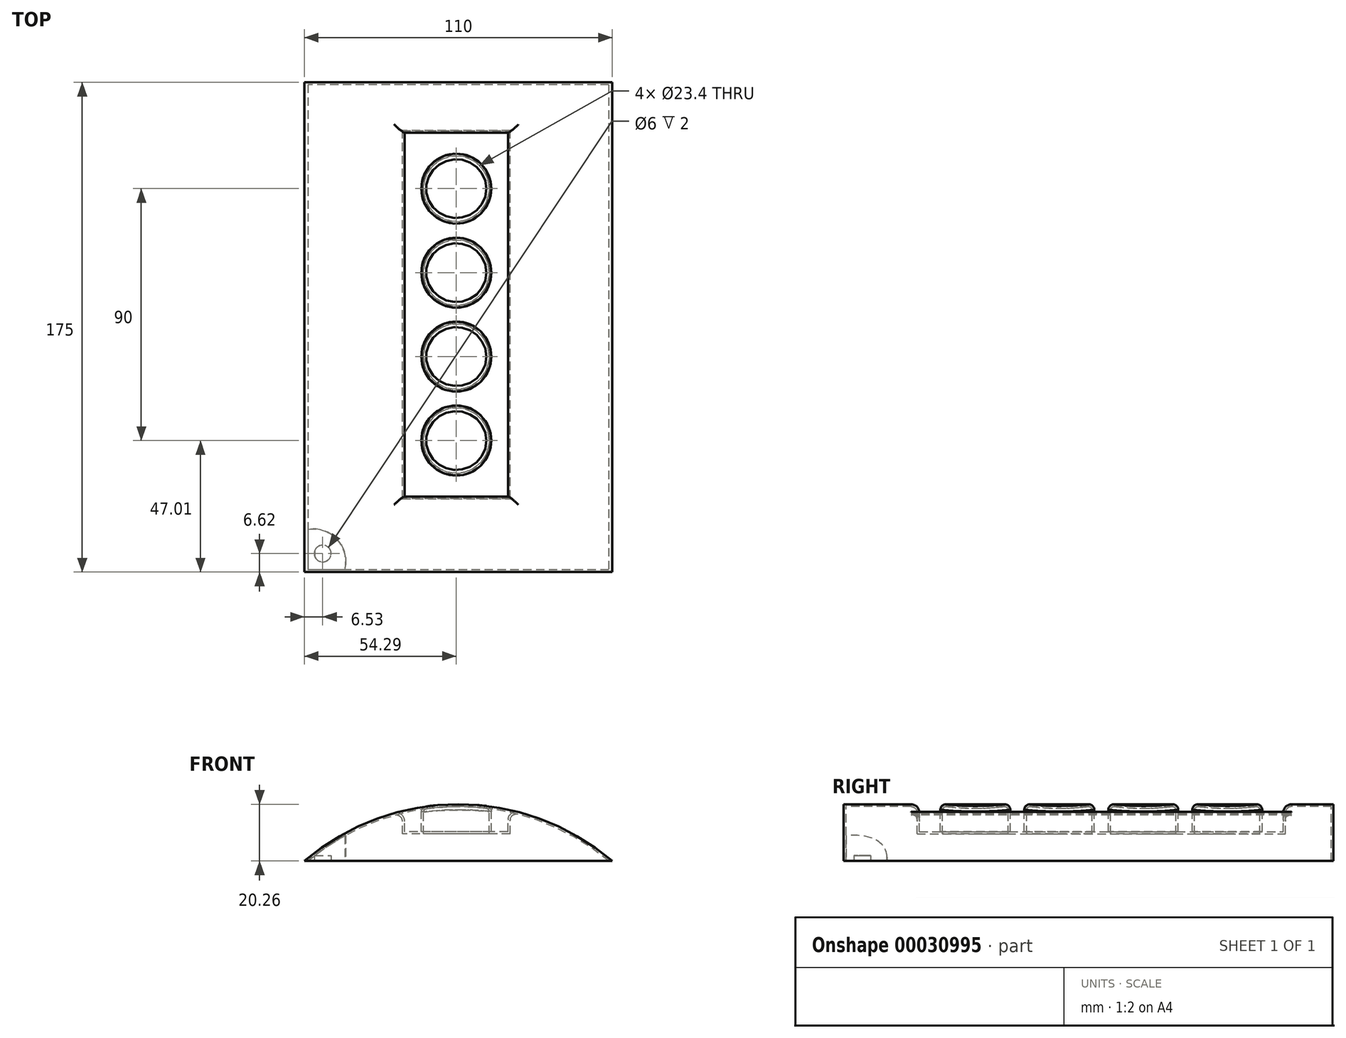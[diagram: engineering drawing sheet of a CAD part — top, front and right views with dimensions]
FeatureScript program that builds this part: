
annotation { "Feature Type Name" : "Feature", "Feature Type Description" : "" }
export const myFeature = defineFeature(function(context is Context, id is Id, definition is map)
    precondition{}
    {
        {
            var Q0;
            Q0=qCreatedBy(makeId("Front.planeOp"),FACE);
            var sketch = newSketch(context, id + "F9", { "sketchPlane" : qUnion([Q0])});
            skLineSegment(sketch, "E0", {"start": v(55.71, 0) * mm, "end": v(-54.29, 0) * mm});
            skLineSegment(sketch, "E1.top", {"start": v(55.71, 20.45) * mm, "end": v(-54.29, 20.45) * mm});
            skLineSegment(sketch, "E1.left", {"start": v(55.71, 0) * mm, "end": v(55.71, 20.45) * mm});
            skLineSegment(sketch, "E1.right", {"start": v(-54.29, 0) * mm, "end": v(-54.29, 20.45) * mm});
            skSolve(sketch);
        }
        {
            var Q0;
            Q0 = qSketchRegion(id + "F9", true);
            extrude(context, id + "F0", {"entities" : qUnion([Q0]), "depth" : 175 * mm});
        }
        {
            var Q0;
            Q0=makeQuery(id+"F0.opExtrude","SWEPT_FACE",FACE,{"disambiguationData":[OSD([sQuery(id+"F9.wireOp",EDGE,"E1.top")])]});
            var sketch = newSketch(context, id + "F1", { "sketchPlane" : qUnion([Q0])});
            skPoint(sketch, "E2.rect.middle", {"position": v(0, -82.99) * mm});
            skLineSegment(sketch, "E3.rect.bottom", {"start": v(18.44, -147.99) * mm, "end": v(-18.44, -147.99) * mm});
            skLineSegment(sketch, "E3.rect.top", {"start": v(18.44, -17.99) * mm, "end": v(-18.44, -17.99) * mm});
            skLineSegment(sketch, "E3.rect.left", {"start": v(18.44, -147.99) * mm, "end": v(18.44, -17.99) * mm});
            skLineSegment(sketch, "E3.rect.right", {"start": v(-18.44, -147.99) * mm, "end": v(-18.44, -17.99) * mm});
            skPoint(sketch, "E2.rect.top.start.orphan", {"position": v(25.94, -17.26) * mm});
            skPoint(sketch, "E2.rect.right.end.orphan", {"position": v(-25.94, -17.26) * mm});
            skPoint(sketch, "E2.rect.bottom.end.orphan", {"position": v(-25.94, -148.72) * mm});
            skPoint(sketch, "E2.rect.bottom.start.orphan", {"position": v(25.94, -148.72) * mm});
            skCircle(sketch, "E4", {"center": v(0, -37.99) * mm, "radius": 12.5 * mm});
            skCircle(sketch, "E5", {"center": v(0, -67.99) * mm, "radius": 12.5 * mm});
            skCircle(sketch, "E6", {"center": v(0, -97.99) * mm, "radius": 12.5 * mm});
            skCircle(sketch, "E7", {"center": v(0, -127.99) * mm, "radius": 12.5 * mm});
            skSolve(sketch);
        }
        {
            var Q0;
            Q0=makeQuery(id+"F1.imprint","IMPRINT",FACE,{"disambiguationData":[TD([[makeQuery(id+"F1.imprint","IMPRINT",EDGE,{"derivedFrom":sQuery(id+"F1.wireOp",EDGE,"E3.rect.bottom")}),-1.0]])]});
            extrude(context, id + "F10", {"entities" : qUnion([Q0]), "operationType" : NewBodyOperationType.REMOVE, "oppositeDirection" : true, "depth" : 10 * mm});
        }
        {
            var Q0;
            Q0=makeQuery(id+"F0.opExtrude","CAP_FACE",FACE,{"disambiguationData":[OSD([sQuery(id+"F9.wireOp",EDGE,"E0"),sQuery(id+"F9.wireOp",EDGE,"E1.top"),sQuery(id+"F9.wireOp",EDGE,"E1.left"),sQuery(id+"F9.wireOp",EDGE,"E1.right")])],"isStart":false});
            var sketch = newSketch(context, id + "F2", { "sketchPlane" : qUnion([Q0])});
            skArc(sketch, "E8", {"start": v(55.71, 0) * mm, "mid": v(0.71, 20.26) * mm, "end": v(-54.29, 0) * mm});
            skSolve(sketch);
        }
        {
            var Q0;
            Q0 = qSketchRegion(id + "F2", true);
            var Q1;
            Q1=makeQuery(id+"F2.imprint","IMPRINT",FACE,{"disambiguationData":[TD([[makeQuery(id+"F2.imprint","IMPRINT",EDGE,{"derivedFrom":sQuery(id+"F2.wireOp",EDGE,"E8")}),-1.0]])]});
            extrude(context, id + "F11", {"entities" : qUnion([Q0, Q1]), "operationType" : NewBodyOperationType.REMOVE, "endBound" : BoundingType.THROUGH_ALL, "oppositeDirection" : true, "depth" : 25 * mm});
        }
        {
            var Q0;
            Q0=makeQuery(id+"F11.boolean.opBoolean","INTERSECT",EDGE,{"derivedFrom":[makeQuery(id+"F10.boolean.opBoolean","COPY",FACE,{"derivedFrom":makeQuery(id+"F10.opExtrude","SWEPT_FACE",FACE,{"disambiguationData":[OSD([sQuery(id+"F1.wireOp",EDGE,"E3.rect.right")])]})}),makeQuery(id+"F11.opExtrude","SWEPT_FACE",FACE,{"disambiguationData":[OSD([sQuery(id+"F2.wireOp",EDGE,"E8")])]})]});
            var Q1;
            Q1=makeQuery(id+"F11.boolean.opBoolean","INTERSECT",EDGE,{"derivedFrom":[makeQuery(id+"F10.boolean.opBoolean","COPY",FACE,{"derivedFrom":makeQuery(id+"F10.opExtrude","SWEPT_FACE",FACE,{"disambiguationData":[OSD([sQuery(id+"F1.wireOp",EDGE,"E3.rect.left")])]})}),makeQuery(id+"F11.opExtrude","SWEPT_FACE",FACE,{"disambiguationData":[OSD([sQuery(id+"F2.wireOp",EDGE,"E8")])]})]});
            var Q2;
            Q2=makeQuery(id+"F11.boolean.opBoolean","INTERSECT",EDGE,{"derivedFrom":[makeQuery(id+"F10.boolean.opBoolean","COPY",FACE,{"derivedFrom":makeQuery(id+"F10.opExtrude","SWEPT_FACE",FACE,{"disambiguationData":[OSD([sQuery(id+"F1.wireOp",EDGE,"E3.rect.top")])]})}),makeQuery(id+"F11.opExtrude","SWEPT_FACE",FACE,{"disambiguationData":[OSD([sQuery(id+"F2.wireOp",EDGE,"E8")])]})]});
            var Q3;
            Q3=makeQuery(id+"F11.boolean.opBoolean","INTERSECT",EDGE,{"derivedFrom":[makeQuery(id+"F10.boolean.opBoolean","COPY",FACE,{"derivedFrom":makeQuery(id+"F10.opExtrude","SWEPT_FACE",FACE,{"disambiguationData":[OSD([sQuery(id+"F1.wireOp",EDGE,"E3.rect.bottom")])]})}),makeQuery(id+"F11.opExtrude","SWEPT_FACE",FACE,{"disambiguationData":[OSD([sQuery(id+"F2.wireOp",EDGE,"E8")])]})]});
            fillet(context, id + "F3", {"entities" : qUnion([Q0, Q1, Q2, Q3]), "radius" : 3 * mm, "tangentPropagation" : true, "allowEdgeOverflow" : false});
        }
        {
            var Q0;
            Q0=makeQuery(id+"F11.boolean.opBoolean","COPY",FACE,{"disambiguationData":[TD([makeQuery(id+"F10.boolean.opBoolean","COPY",FACE,{"derivedFrom":makeQuery(id+"F10.opExtrude","SWEPT_FACE",FACE,{"disambiguationData":[OSD([sQuery(id+"F1.wireOp",EDGE,"E7")])]})})])],"derivedFrom":makeQuery(id+"F11.opExtrude","SWEPT_FACE",FACE,{"disambiguationData":[OSD([sQuery(id+"F2.wireOp",EDGE,"E8")])]})});
            var Q1;
            Q1=makeQuery(id+"F11.boolean.opBoolean","COPY",FACE,{"disambiguationData":[TD([makeQuery(id+"F10.boolean.opBoolean","COPY",FACE,{"derivedFrom":makeQuery(id+"F10.opExtrude","SWEPT_FACE",FACE,{"disambiguationData":[OSD([sQuery(id+"F1.wireOp",EDGE,"E6")])]})})])],"derivedFrom":makeQuery(id+"F11.opExtrude","SWEPT_FACE",FACE,{"disambiguationData":[OSD([sQuery(id+"F2.wireOp",EDGE,"E8")])]})});
            var Q2;
            Q2=makeQuery(id+"F11.boolean.opBoolean","COPY",FACE,{"disambiguationData":[TD([makeQuery(id+"F10.boolean.opBoolean","COPY",FACE,{"derivedFrom":makeQuery(id+"F10.opExtrude","SWEPT_FACE",FACE,{"disambiguationData":[OSD([sQuery(id+"F1.wireOp",EDGE,"E5")])]})})])],"derivedFrom":makeQuery(id+"F11.opExtrude","SWEPT_FACE",FACE,{"disambiguationData":[OSD([sQuery(id+"F2.wireOp",EDGE,"E8")])]})});
            var Q3;
            Q3=makeQuery(id+"F11.boolean.opBoolean","COPY",FACE,{"disambiguationData":[TD([makeQuery(id+"F10.boolean.opBoolean","COPY",FACE,{"derivedFrom":makeQuery(id+"F10.opExtrude","SWEPT_FACE",FACE,{"disambiguationData":[OSD([sQuery(id+"F1.wireOp",EDGE,"E4")])]})})])],"derivedFrom":makeQuery(id+"F11.opExtrude","SWEPT_FACE",FACE,{"disambiguationData":[OSD([sQuery(id+"F2.wireOp",EDGE,"E8")])]})});
            fillet(context, id + "F4", {"entities" : qUnion([Q0, Q1, Q2, Q3]), "radius" : 2 * mm, "tangentPropagation" : true, "allowEdgeOverflow" : false});
        }
        {
            var Q0;
            Q0=makeQuery(id+"F0.opExtrude","SWEPT_FACE",FACE,{"disambiguationData":[OSD([sQuery(id+"F9.wireOp",EDGE,"E0")])]});
            shell(context, id + "F12", {"entities" : qUnion([Q0]), "thickness" : 0.8 * mm});
        }
        {
            var Q0;
            Q0=makeQuery(id+"F0.opExtrude","SWEPT_FACE",FACE,{"disambiguationData":[OSD([sQuery(id+"F9.wireOp",EDGE,"E0")])]});
            var sketch = newSketch(context, id + "F5", { "sketchPlane" : qUnion([Q0])});
            skArc(sketch, "E9", {"start": v(-53.05, 159.7) * mm, "mid": v(-42.56, 163.41) * mm, "end": v(-39.86, 174.2) * mm});
            skLineSegment(sketch, "E10", {"start": v(-53.05, 174.2) * mm, "end": v(-53.05, 159.7) * mm});
            skLineSegment(sketch, "E11", {"start": v(-53.05, 159.7) * mm, "end": v(-53.05, 174.2) * mm});
            skLineSegment(sketch, "E12", {"start": v(-53.05, 174.2) * mm, "end": v(-39.86, 174.2) * mm});
            skLineSegment(sketch, "E13", {"start": v(0.95, 175.1) * mm, "end": v(0.95, 187.91) * mm});
            skArc(sketch, "E14.MirrorCS", {"start": v(54.95, 159.7) * mm, "mid": v(44.47, 163.41) * mm, "end": v(41.76, 174.2) * mm});
            skLineSegment(sketch, "E15.MirrorCS", {"start": v(54.95, 174.2) * mm, "end": v(41.76, 174.2) * mm});
            skLineSegment(sketch, "E16.MirrorCS", {"start": v(54.95, 159.7) * mm, "end": v(54.95, 174.2) * mm});
            skSolve(sketch);
        }
        {
            var Q0;
            Q0=makeQuery(id+"F5.imprint","IMPRINT",FACE,{"disambiguationData":[TD([[makeQuery(id+"F5.imprint","IMPRINT",EDGE,{"derivedFrom":sQuery(id+"F5.wireOp",EDGE,"E9")}),1.0]])]});
            var Q1;
            {var subQ0=sQuery(id+"F9.wireOp",EDGE,"E0");var subQ2=sQuery(id+"F5.wireOp",EDGE,"E14.MirrorCS");var subQ4=sQuery(id+"F5.wireOp",EDGE,"E15.MirrorCS");var subQ6=makeQuery(id+"F5.imprint","INTERSECT",VERTEX,{"derivedFrom":[makeQuery(id+"F12.opShell","OFFSET_EDGE",EDGE,{"disambiguationData":[OSD([subQ0]),TDD([makeQuery(id+"F0.opExtrude","CAP_EDGE",EDGE,{"disambiguationData":[OSD([subQ0])],"isStart":false})])]}),subQ2,subQ4]});Q1=makeQuery(id+"F5.imprint","IMPRINT",FACE,{"disambiguationData":[TD([[makeQuery(id+"F5.imprint","IMPRINT",EDGE,{"disambiguationData":[TD([[subQ6,1.0]])],"derivedFrom":subQ2}),-1.0]])]});}
            extrude(context, id + "F6", {"entities" : qUnion([Q0, Q1]), "endBound" : BoundingType.UP_TO_NEXT, "oppositeDirection" : true, "depth" : 25 * mm});
        }
        {
            var Q0;
            Q0=makeQuery(id+"F6.opExtrude","CAP_FACE",FACE,{"disambiguationData":[OSD([sQuery(id+"F5.wireOp",EDGE,"E9"),sQuery(id+"F5.wireOp",EDGE,"E11"),sQuery(id+"F5.wireOp",EDGE,"E12")])],"isStart":true});
            var sketch = newSketch(context, id + "F7", { "sketchPlane" : qUnion([Q0])});
            skPoint(sketch, "E17.center.orphan", {"position": v(-42.56, 163.41) * mm});
            skCircle(sketch, "E18", {"center": v(-47.76, 168.38) * mm, "radius": 3 * mm});
            skCircle(sketch, "E19", {"center": v(48.4, 168.2) * mm, "radius": 3 * mm});
            skSolve(sketch);
        }
        {
            var Q0;
            Q0 = qSketchRegion(id + "F7", true);
            extrude(context, id + "F8", {"entities" : qUnion([Q0]), "operationType" : NewBodyOperationType.REMOVE, "oppositeDirection" : true, "depth" : 2 * mm});
        }
    });
